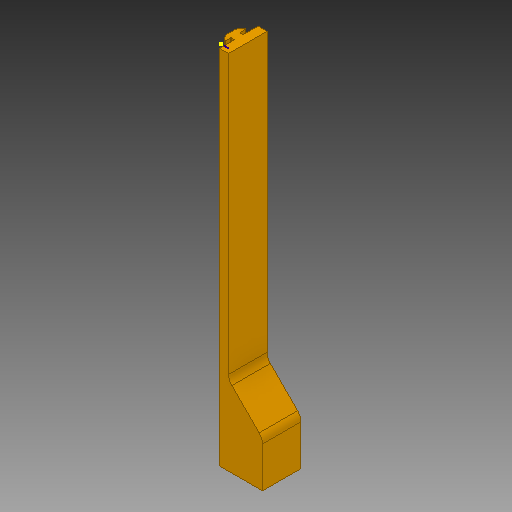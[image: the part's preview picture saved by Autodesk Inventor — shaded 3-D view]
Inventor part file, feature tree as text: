
AUTODESK INVENTOR PART (.ipt)
format: ipt  version: 2017 (Build 210142000, 142)  size: 225,280 bytes
history: native  units: in
note: dims shown in document units (in); Inventor stores cm internally (conversion verified against a paired STEP export)
features: sketch x7, extrude x6, fillet x3, other x1, plane x1, chamfer x1
ambient origin geometry x8: Origin, YZ Plane, XZ Plane, XY Plane, X Axis, Y Axis, Z Axis, Center Point
bodies: Solid1 (feature_tree)
feature tree (19):
  other  "20X20Connector"
  extrude  "Extrusion1"  Depth=1.0in
  plane  "Work Plane1"
  fillet  "Fillet2"  Radius=1.0in
  extrude  "Extrusion2"  Depth=7.0in TaperAngle=0.0deg
  sketch  "Sketch3"  dims[d22=0.1in d23=0.0in d24=0.0156in d25=1.0in]
  extrude  "Extrusion3"  Depth=0.0156in
  fillet  "Fillet3"  Radius=1.0in
  extrude  "Extrusion4"  Depth=0.75in TaperAngle=45.0deg
  chamfer  "Chamfer1"  Distance=0.1in
  extrude  "Extrusion5"  Depth=0.25in
  extrude  "Extrusion6"  [1 undecoded]
  fillet  "Fillet4"  [1 undecoded]
  sketch  "Sketch1"  dims[d0=0.0984in d1=0.0787in d2=0.1874in d3=0.4524in d4=0.1085in d5=0.225in d6=0.2221in d7=0.2313in d8=0.03in d9=0.03in d11=0.9949in d12=0.1137in d13=0.6693in d14=0.65in d15=1.0in d16=0.0in]
  sketch  "Sketch2"  dims[d17=0.0in d19=0.0156in d20=7.0in d21=0.0in]
  sketch  "Sketch4"  dims[d26=0.75in d27=0.0in d28=0.75in d29=0.125in d30=45.0deg d31=0.1in d32=0.0in]
  sketch  "Sketch5"  dims[d33=0.1in d34=0.0in d35=0.25in]
  sketch  "Sketch6"
  sketch  "Sketch7"
note: 2 required parameter values undecoded (feature->parameter linkage not recoverable at this tier; creation-order binding heuristic only, values carry confidence <= 0.55)
